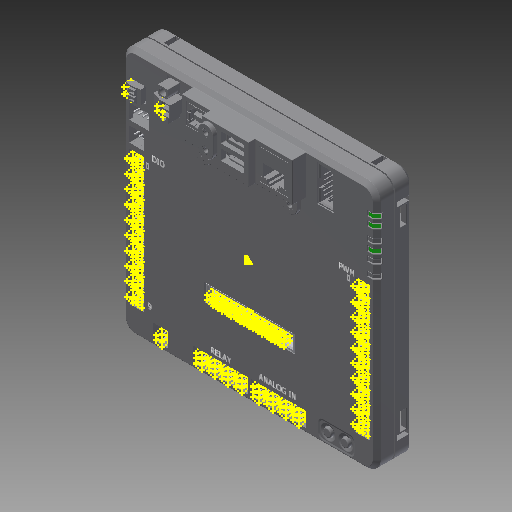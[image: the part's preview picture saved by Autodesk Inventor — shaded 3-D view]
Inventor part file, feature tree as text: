
AUTODESK INVENTOR PART (.ipt)
format: ipt  version: 2019 (Build 230136000, 136)  size: 38,559,744 bytes
history: native  units: in
note: dims shown in document units (in); Inventor stores cm internally (conversion verified against a paired STEP export)
features: other x76, imported_body x16, sketch x1
ambient origin geometry x8: Origin, YZ Plane, XZ Plane, XY Plane, X Axis, Y Axis, Z Axis, Center Point
bodies: Solid1 (feature_tree), Solid2 (feature_tree), Solid3 (feature_tree), Solid4 (feature_tree), Solid5 (feature_tree), Solid6 (feature_tree), Solid7 (feature_tree), Solid8 (feature_tree), Solid9 (feature_tree), Solid10 (feature_tree), Solid11 (feature_tree), Solid12 (feature_tree), Solid13 (feature_tree), Solid14 (feature_tree), Solid15 (feature_tree), Solid16 (feature_tree)
feature tree (93):
  other  "cd_roborio1"
  other  "D10"
  other  "D11"
  other  "D12"
  other  "D13"
  other  "D14"
  other  "D15"
  other  "D16"
  other  "D17"
  other  "D18"
  other  "D19"
  other  "D20"
  other  "D21"
  other  "D22"
  other  "D23"
  other  "D24"
  other  "D25"
  other  "D26"
  other  "D27"
  other  "D28"
  other  "D29"
  other  "D30"
  other  "P10"
  other  "P11"
  other  "P12"
  other  "P13"
  other  "P14"
  other  "P15"
  other  "P16"
  other  "P17"
  other  "P18"
  other  "P19"
  other  "P20"
  other  "P21"
  other  "P22"
  other  "P23"
  other  "P24"
  other  "P25"
  other  "P26"
  other  "P27"
  other  "P28"
  other  "P29"
  other  "P30"
  other  "RSL1"
  other  "RSL2"
  other  "R10"
  other  "R11"
  other  "R12"
  other  "A10"
  other  "A11"
  other  "A12"
  other  "X10"
  other  "X11"
  other  "X12"
  other  "X13"
  other  "X14"
  other  "X15"
  other  "X16"
  other  "X17"
  other  "X18"
  other  "X19"
  other  "X20"
  other  "X21"
  other  "X22"
  other  "X23"
  other  "X24"
  other  "X25"
  other  "X26"
  other  "X27"
  other  "X28"
  other  "X29"
  other  "X30"
  other  "X31"
  other  "X32"
  other  "X33"
  other  "X34"
  sketch  "Sketch1"
  imported_body  "Base1"
  imported_body  "Base2"
  imported_body  "Base3"
  imported_body  "Base4"
  imported_body  "Base5"
  imported_body  "Base6"
  imported_body  "Base7"
  imported_body  "Base8"
  imported_body  "Base9"
  imported_body  "Base10"
  imported_body  "Base11"
  imported_body  "Base12"
  imported_body  "Base13"
  imported_body  "Base14"
  imported_body  "Base15"
  imported_body  "Base16"
